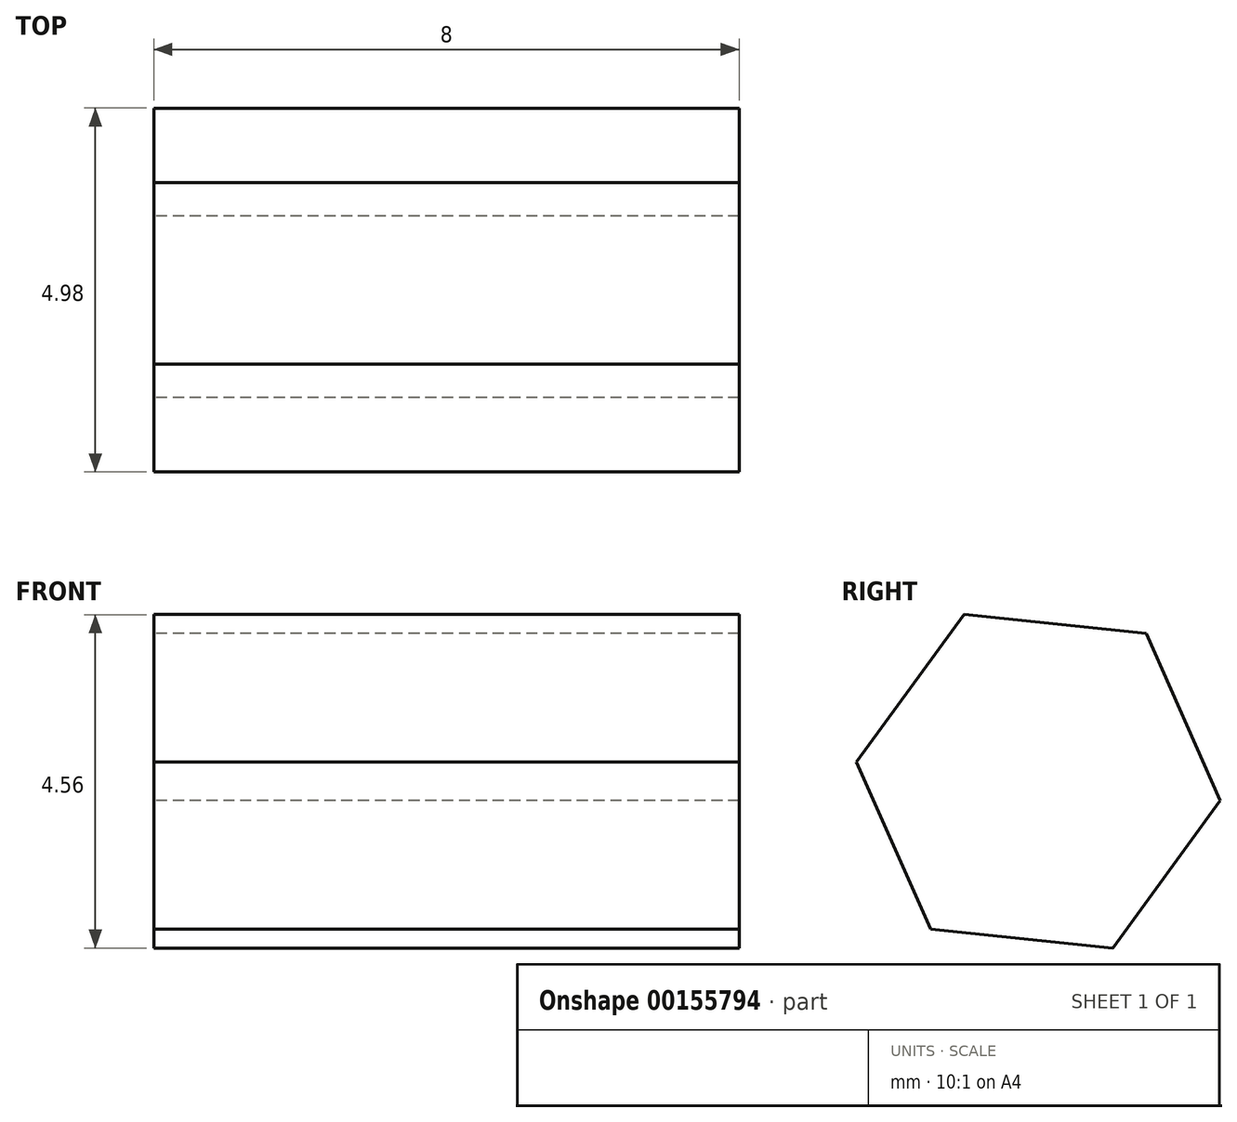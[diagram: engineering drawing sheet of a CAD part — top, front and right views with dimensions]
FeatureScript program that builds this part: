
annotation { "Feature Type Name" : "Feature", "Feature Type Description" : "" }
export const myFeature = defineFeature(function(context is Context, id is Id, definition is map)
    precondition{}
    {
        {
            var Q0;
            Q0=qCreatedBy(makeId("Right.planeOp"),FACE);
            var sketch = newSketch(context, id + "F0", { "sketchPlane" : qUnion([Q0])});
            skCircle(sketch, "E0", {"center": v(0, 0) * mm, "radius": 2.5 * mm});
            skCircle(sketch, "E1.cCircle", {"center": v(0, 0) * mm, "radius": 2.5 * mm, "construction": true});
            skLineSegment(sketch, "E1.0", {"start": v(2.49, -0.26) * mm, "end": v(1.01, -2.28) * mm});
            skLineSegment(sketch, "E1.1", {"start": v(1.01, -2.28) * mm, "end": v(-1.47, -2.02) * mm});
            skLineSegment(sketch, "E1.2", {"start": v(-1.47, -2.02) * mm, "end": v(-2.49, 0.26) * mm});
            skLineSegment(sketch, "E1.3", {"start": v(-2.49, 0.26) * mm, "end": v(-1.01, 2.28) * mm});
            skLineSegment(sketch, "E1.4", {"start": v(-1.01, 2.28) * mm, "end": v(1.47, 2.02) * mm});
            skLineSegment(sketch, "E1.5", {"start": v(1.47, 2.02) * mm, "end": v(2.49, -0.26) * mm});
            skSolve(sketch);
        }
        {
            var Q0;
            Q0=makeQuery(id+"F0.imprint","IMPRINT",FACE,{"disambiguationData":[TD([[makeQuery(id+"F0.imprint","IMPRINT",EDGE,{"derivedFrom":sQuery(id+"F0.wireOp",EDGE,"E1.0")}),-1.0]])]});
            extrude(context, id + "F1", {"entities" : qUnion([Q0]), "depth" : 8 * mm});
        }
    });
